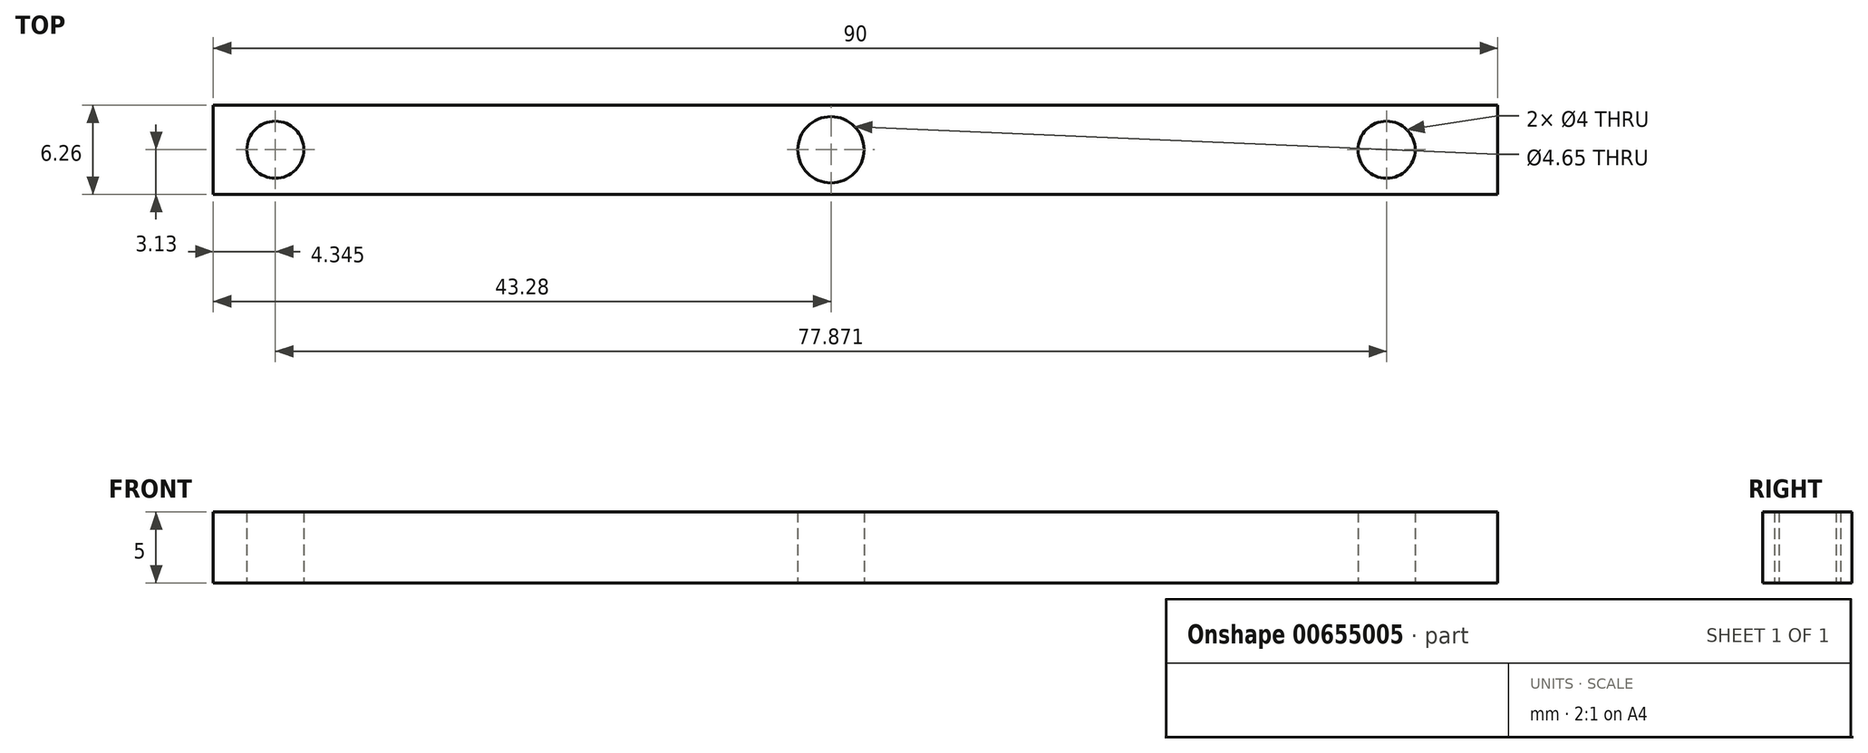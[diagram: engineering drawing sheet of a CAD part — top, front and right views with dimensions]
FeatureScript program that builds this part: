
annotation { "Feature Type Name" : "Feature", "Feature Type Description" : "" }
export const myFeature = defineFeature(function(context is Context, id is Id, definition is map)
    precondition{}
    {
        {
            var Q0;
            Q0=qCreatedBy(makeId("Top.planeOp"),FACE);
            var sketch = newSketch(context, id + "F0", { "sketchPlane" : qUnion([Q0])});
            skLineSegment(sketch, "E0.bottom", {"start": v(46.72, 3.13) * mm, "end": v(-43.28, 3.13) * mm});
            skLineSegment(sketch, "E0.top", {"start": v(46.72, -3.13) * mm, "end": v(-43.28, -3.13) * mm});
            skLineSegment(sketch, "E0.left", {"start": v(46.72, 3.13) * mm, "end": v(46.72, -3.13) * mm});
            skLineSegment(sketch, "E0.right", {"start": v(-43.28, 3.13) * mm, "end": v(-43.28, -3.13) * mm});
            skPoint(sketch, "E0.middle", {"position": v(1.72, 0) * mm});
            skCircle(sketch, "E1", {"center": v(-38.94, 0) * mm, "radius": 2 * mm});
            skCircle(sketch, "E2.MirrorC", {"center": v(38.94, 0) * mm, "radius": 2 * mm});
            skCircle(sketch, "E3", {"center": v(0, 0) * mm, "radius": 2.32 * mm});
            skSolve(sketch);
        }
        {
            var Q0;
            Q0=makeQuery(id+"F0.imprint","IMPRINT",FACE,{"disambiguationData":[TD([[makeQuery(id+"F0.imprint","IMPRINT",EDGE,{"derivedFrom":sQuery(id+"F0.wireOp",EDGE,"E0.bottom")}),1.0]])]});
            extrude(context, id + "F1", {"entities" : qUnion([Q0]), "depth" : 5 * mm, "offsetDistance" : 25 * mm});
        }
    });
